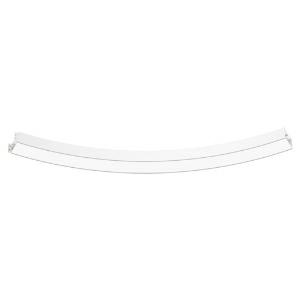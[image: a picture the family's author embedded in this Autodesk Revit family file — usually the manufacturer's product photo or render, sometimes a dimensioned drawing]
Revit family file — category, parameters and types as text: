
# Revit family: super-g_super-g__5400___51deg_hl_led__36_8w_5680lm_3000k_cri_80_430-1160_54d3
name_source: partatom
category: Leuchten
revit_build: Autodesk Revit 2016 (Build: 20190508_0715(x64)
units: mm (PartAtom-declared; Revit-internal decimal feet)

## family parameters
Basisbauteil = Fläche
Beim Laden mit Abzugskörper schneiden = Nein
Bemaßung runder Anschluss = Durchmesser verwenden
Gemeinsam genutzt = Nein
Lichtquelle = Nein
Raumberechnungspunkt = Nein
Teiletyp = Normal

## types (1)
- 430-1160- (1 x LED, 710 lm, 3000K)
    Approval mark = CE
    Beschreibung = The insert consists of aluminum-extruded profile. Charming SOFT-EDGE design ensure unparalleled styling. The ballast is integrated and allows for an operation with 220-240V (50/60Hz). SUPER-G (# 430-1160) ist not dimmable (on/off).
    CIE Flux Codes = 44 75 94 100 65
    Color Rendering = 1B/80…89
    Color Temperature = 3000K
    Height = 120 mm
    Hersteller = Prolicht
    Lamp Light Flux = 710 lm
    Lamp count = 1
    Lampe = 1 x LED
    Length = 300 mm
    Luminous efficacy = 90 lm/W
    ModVariant = Nein
    Modell = 430-1160
    Mounting Place = Ceiling
    Mounting Type = Pendant
    Number of Poles = 1
    OnlyDefault = Ja
    Power Factor = 1
    Product Name = SUPER-G__SUPER-G  5400 / 51° HL LED: 36,8W 5680lm 3000K CRI:80
    Product group = Suspended profile systems
    ProductGroupID = 944
    Protection Class = Protection class I
    Protection Degree = IP 20
    RLX_Detail_Level = 1
    RlxData = <blob elided: 27901 chars, md5=3f31f25b>
    Scheinlast = 41 VA
    Socket = socket
    Standby Power = 0 W
    System Light Flux = 3692 lm
    System Power = 41 W
    Typenbild = 430-1160.jpg
    URL = http://relux.com
    VarID = 430-1160-
    Voltage = 0 V
    Vorgabe-Ansicht = 1800 mm
    Weight = 0.00 kg
    Width = 150 mm

## geometry (parser evidence)
native form markers: Blend x4, Sweep x28
no freeform markers — native parametric forms only
